# Revit family: Backflow_Preventer-RP-Zurn_Wilkins-Model_950XL3BFSS-(114-2_inch)
name_source: partatom
category: Pipe Accessories
units: mm (PartAtom-declared; Revit-internal decimal feet)

## family parameters
Always vertical = Yes
Cut with Voids When Loaded = No
OmniClass Number = 23.65.55.14.17
OmniClass Title = Adjusting/Controlling Valves for Liquid Services
Part Type = Valve - Breaks Into
Round Connector Dimension = Use Radius
Shared = No
Work Plane-Based = No

## types (3) — shared parameters
Assembly Code = D2020300
BF center = 0' - 0 25/32"
BODY FL BOLT HT = 0' - 0 1/8"
BODY FL HT = 0' - 0 1/4"
BODY FL RADIUS = 0' - 0 9/16"
CB L3 = 0' - 0 1/4"
CB L4 = 0' - 0 1/8"
CB TC DIA1 = 0' - 0 3/8"
CB TC DIA2 = 0' - 0 13/16"
CB TC DIA3 = 0' - 0 3/8"
DIM E - Height (Valve Center to Bottom of relief valve) = 0' - 2 3/4"
Default Elevation = 0' - 0"
Description = Reduced Pressure Principle Assembly
Flow Rate (GPM) = 0 GPM
Hydrostatic Test Pressure = 350.00 psi
LBFV Width = 0' - 3 11/16"
LE to Bf = 0' - 0 5/32"
LEFT BLEND START = 0' - 0 7/16"
Main Material = Paint - Zurn - Bronze
Manufacturer = Zurn Water, LLC
Manufacturer Brand = Zurn Wilkins
Max Working Water Pressure = 175.00 psi
Max Working Water Temperature = 180 °F
Model = 950XL3BFSS
Modified Date = 10/17/25
Product Documentation Link = https://files.zurn.com
Product Installation Sheet URL = https://files.zurn.com
Product Page URL = https://www.zurn.com
Product data URL = https://bimobject.com
REL COV BOLT LG = 0' - 0 1/4"
REL COV REC WID = 0' - 1 5/16"
RIGHT LOFT END = 0' - 1"
RP END = 0' - 4 5/32"
RP FLANGE END = 0' - 0 29/32"
RP PIPE 2 = 0' - 1 1/4"
RP PIPE DIA = 0' - 1"
RP REC THICK = 0' - 1"
RP REC WIDTH = 0' - 1"
Repair Parts URL = https://files.zurn.com
TC H1 = 0' - 1 1/2"
TC H2 = 0' - 0 1/4"
TC H3 = 0' - 1 1/8"
TC RADIUS 1 = 0' - 0 13/32"
TC RADIUS 2 = 0' - 0 3/16"
TC STEM CENTER = 0' - 0 5/8"
TC STEM DIA = 0' - 0 1/2"
TC STEM HT = 0' - 0 17/32"
URL = https://www.zurn.com

## per-type parameters (varying)
- 114-950XL3BFSS (1-1/4" 950XL3BFSS): BFEE=0' - 0 5/16"; BFV Dis=0' - 0"; BFV WIDTH=0' - 3 25/32"; BFVE=0' - 2 1/4"; BODY FL BOLT DIA=0' - 0 9/32"; BODY FL BOLT L1=0' - 2 7/16"; BODY FL BOLT L2=0' - 2 5/8"; BODY FL WID=0' - 3 7/32"; BODY RIB LINE=0' - 2 1/2"; BODY RIB PATH END=0' - 2 1/32"; BODY RIB PATH L1=0' - 1 5/16"; BODY RIB THICK=0' - 0 3/16"; BODY RIB WIDTH=0' - 2 1/4"; BODY TC STEM CENTER=0' - 6"; BTM RIB END=0' - 0 13/32"; BV DIA-1=0' - 1 1/2"; BV DIA-2=0' - 2 1/8"; BV DIA-3=0' - 2 5/16"; BV HEX LENGTH=0' - 0 9/16"; BV HEX WIDTH=0' - 1 29/32"; BV L1=0' - 0 3/4"; BV L2=0' - 1"; BV LENGTH=0' - 3 11/16"; BV RIB HT=0' - 1 1/4"; BV RIB START=0' - 0 1/2"; BV RIB THICK=0' - 0 1/2"; BV RIB WIDTH=0' - 1 13/16"; Butterfly Valve=Fire_Valve-Zurn_Wilkins-Model_F49BR-(114-2_inch) : 114-F49BR (1 1/4" F49BR); CB L1=0' - 0 3/4"; CB L2=0' - 4 1/2"; CB LARGE DIA=0' - 3 1/4"; CB SMALL DIA=0' - 2 1/2"; CB START=0' - 2"; CENTER-END=0' - 7 25/32"; DIM A - Total Length=1' - 1 1/2"; DIM B - Width (Valve end to Valve center)=0' - 3 5/16"; DIM C - Width (Valve center to Valve End)=0' - 1 5/8"; DIM D - Height (Valve Center to top of test cock)=0' - 4 5/16"; HANDLE BASE HT=0' - 2"; HANDLE H1=0' - 0 3/8"; HANDLE HEIGHT=0' - 1"; HANDLE NUT WIDTH=0' - 0 5/8"; HANDLE THICKNESS=0' - 0 1/8"; HANDLE V1=0' - 0 7/8"; HANDLE V2=0' - 5"; LE TO LBFV=0' - 0 1/4"; LEFT BELND LH DIA=0' - 2 5/8"; LEFT BELND RH DIA=0' - 3 1/8"; Length=1' - 3 9/16"; MASKING VER1=0' - 2 3/8"; MASKING VER2=0' - 3"; MR ball valve handle hex width=0' - 0 23/32"; MR left end to ball valve handle-1=0' - 2 9/32"; MR left end to ball valve handle-2=0' - 2 21/32"; MR left end to ball valve handle-3=0' - 2 23/32"; MR left end to main valve-1=0' - 6 5/32"; MR left end to main valve-2=0' - 4 13/16"; MR main valve body diameter-1=0' - 3 1/4"; MR main valve body width-1=0' - 3 31/32"; MR right end to ball valve handle-1=0' - 2 11/32"; MR right end to ball valve handle-2=0' - 2 23/32"; MR right end to ball valve handle-3=0' - 2 25/32"; MR right end to main valve-1=0' - 4 1/2"; MR right end to main valve-2=0' - 4 19/32"; MR valve body diameter-1=0' - 2 5/16"; MR valve body diameter-2=0' - 2 1/8"; MR valve body diameter-3=0' - 1 3/4"; MR valve body diameter-4=0' - 1 1/2"; MR valve center to ball valve handle-1=0' - 1 7/8"; MR valve center to ball valve handle-2=0' - 2 1/16"; MR valve center to ball valve handle-3=0' - 2 5/16"; MR valve center to ball valve handle-4=0' - 2 7/16"; Nominal Diameter=0' - 1 1/4"; Nominal Radius=0' - 0 5/8"; PIPE DIA=0' - 1 1/2"; PIPE RADIUS END=0' - 3 1/16"; Product Weight (lbs)=12; RBFE=0' - 0 13/16"; RBFV Width=0' - 3 19/32"; RBFVE=0' - 3 1/2"; RE to RBFV=0' - 0 3/8"; REL COV BOLT DIA=0' - 0 5/16"; REL COV BOLT HOR C-C=0' - 1 7/8"; REL COV BOLT HOR2 C-C=0' - 3 1/4"; REL COV BOLT VER C-C=0' - 2 3/4"; REL COV REC HT=0' - 1"; RP BTM PIPE DIA=0' - 1 1/8"; RP BTM PIPE L1=0' - 1 1/8"; RP BTM PIPE PLANE=0' - 0 7/8"; RP CENTER=0' - 3 15/32"; RP FLANGE START=0' - 1"; RP LOFT LEFT DIA=0' - 2 7/8"; RP LOFT RIGHT DIA=0' - 1 3/4"; RP REC HT=0' - 1 11/16"; RP START=0' - 4 1/4"; RPC-E=0' - 1 23/32"; TC BASE DIA=0' - 0 3/4"; TC BASE HT=0' - 1 3/8"; TC CENTER=0' - 1 3/4"; TC1 BASE DIA=0' - 0 3/4"; TC1-CENTER=0' - 0 15/16"; TC2 CENTER=0' - 0 5/8"; TC2 STEM CENTER=0' - 3 7/32"; Top Width=0' - 1 1/2"
- 112-950XL3BFSS (1-1/2" 950XL3BFSS): BFEE=0' - 0 1/16"; BFV Dis=0' - 0 1/16"; BFV WIDTH=0' - 3 25/32"; BFVE=0' - 2 1/8"; BODY FL BOLT DIA=0' - 0 9/32"; BODY FL BOLT L1=0' - 2 3/8"; BODY FL BOLT L2=0' - 2 3/8"; BODY FL WID=0' - 3"; BODY RIB LINE=0' - 2 1/2"; BODY RIB PATH END=0' - 1 7/8"; BODY RIB PATH L1=0' - 1 1/4"; BODY RIB THICK=0' - 0 3/16"; BODY RIB WIDTH=0' - 2 1/4"; BODY TC STEM CENTER=0' - 6"; BTM RIB END=0' - 0 13/32"; BV DIA-1=0' - 1 3/4"; BV DIA-2=0' - 2 3/8"; BV DIA-3=0' - 2 9/16"; BV HEX LENGTH=0' - 0 21/32"; BV HEX WIDTH=0' - 2 3/16"; BV L1=0' - 0 5/8"; BV L2=0' - 1 1/8"; BV LENGTH=0' - 4"; BV RIB HT=0' - 1 7/16"; BV RIB START=0' - 0 5/8"; BV RIB THICK=0' - 0 9/16"; BV RIB WIDTH=0' - 2"; Butterfly Valve=Fire_Valve-Zurn_Wilkins-Model_F49BR-(114-2_inch) : 112-F49BR (1 1/2" F49BR); CB L1=0' - 0 5/8"; CB L2=0' - 4 5/8"; CB LARGE DIA=0' - 3"; CB SMALL DIA=0' - 2 1/2"; CB START=0' - 2"; CENTER-END=0' - 7 27/32"; DIM A - Total Length=1' - 1 7/8"; DIM B - Width (Valve end to Valve center)=0' - 3 7/16"; DIM C - Width (Valve center to Valve End)=0' - 1 5/8"; DIM D - Height (Valve Center to top of test cock)=0' - 4 5/16"; HANDLE BASE HT=0' - 2 1/2"; HANDLE H1=0' - 0 7/16"; HANDLE HEIGHT=0' - 1"; HANDLE NUT WIDTH=0' - 0 3/4"; HANDLE THICKNESS=0' - 0 1/8"; HANDLE V1=0' - 1"; HANDLE V2=0' - 5"; LE TO LBFV=0' - 0 1/4"; LEFT BELND LH DIA=0' - 2 5/8"; LEFT BELND RH DIA=0' - 3 1/8"; Length=1' - 3 11/16"; MASKING VER1=0' - 2 1/4"; MASKING VER2=0' - 3 5/16"; MR ball valve handle hex width=0' - 0 7/8"; MR left end to ball valve handle-1=0' - 2 3/8"; MR left end to ball valve handle-2=0' - 2 13/16"; MR left end to ball valve handle-3=0' - 2 7/8"; MR left end to main valve-1=0' - 6 13/32"; MR left end to main valve-2=0' - 5 1/16"; MR main valve body diameter-1=0' - 3 5/32"; MR main valve body width-1=0' - 3 31/32"; MR right end to ball valve handle-1=0' - 2 11/16"; MR right end to ball valve handle-2=0' - 3 1/8"; MR right end to ball valve handle-3=0' - 3 3/16"; MR right end to main valve-1=0' - 4 3/8"; MR right end to main valve-2=0' - 4 9/16"; MR valve body diameter-1=0' - 2 9/16"; MR valve body diameter-2=0' - 2 3/8"; MR valve body diameter-3=0' - 1 7/8"; MR valve body diameter-4=0' - 1 3/4"; MR valve center to ball valve handle-1=0' - 2 3/8"; MR valve center to ball valve handle-2=0' - 2 9/16"; MR valve center to ball valve handle-3=0' - 2 7/8"; MR valve center to ball valve handle-4=0' - 3"; Nominal Diameter=0' - 1 1/2"; Nominal Radius=0' - 0 3/4"; PIPE DIA=0' - 1 3/4"; PIPE RADIUS END=0' - 3 1/16"; Product Weight (lbs)=14; RBFE=0' - 0 19/32"; RBFV Width=0' - 3"; RBFVE=0' - 3"; RE to RBFV=0' - 0 7/16"; REL COV BOLT DIA=0' - 0 5/16"; REL COV BOLT HOR C-C=0' - 1 7/8"; REL COV BOLT HOR2 C-C=0' - 3 1/4"; REL COV BOLT VER C-C=0' - 2 3/4"; REL COV REC HT=0' - 1 1/8"; RP BTM PIPE DIA=0' - 1 1/8"; RP BTM PIPE L1=0' - 1 1/4"; RP BTM PIPE PLANE=0' - 0 7/8"; RP CENTER=0' - 3 15/32"; RP FLANGE START=0' - 1"; RP LOFT LEFT DIA=0' - 2 7/8"; RP LOFT RIGHT DIA=0' - 1 3/4"; RP REC HT=0' - 1 11/16"; RP START=0' - 4 1/2"; RPC-E=0' - 1 23/32"; TC BASE DIA=0' - 0 3/4"; TC BASE HT=0' - 1 7/16"; TC CENTER=0' - 1 3/4"; TC1 BASE DIA=0' - 0 3/4"; TC1-CENTER=0' - 1 1/8"; TC2 CENTER=0' - 0 3/4"; TC2 STEM CENTER=0' - 3 3/16"; Top Width=0' - 1 17/32"
- 2-950XL3BFSS (2" 950XL3BFSS): BFEE=0' - 0 1/32"; BFV Dis=0' - 0 1/4"; BFV WIDTH=0' - 3"; BFVE=0' - 1 31/32"; BODY FL BOLT DIA=0' - 0 3/8"; BODY FL BOLT L1=0' - 2 7/8"; BODY FL BOLT L2=0' - 2 7/8"; BODY FL WID=0' - 3 1/2"; BODY RIB LINE=0' - 3 1/4"; BODY RIB PATH END=0' - 2 9/16"; BODY RIB PATH L1=0' - 1 3/8"; BODY RIB THICK=0' - 0 1/4"; BODY RIB WIDTH=0' - 2"; BODY TC STEM CENTER=0' - 7 5/32"; BTM RIB END=0' - 1 1/8"; BV DIA-1=0' - 2 1/4"; BV DIA-2=0' - 2 7/8"; BV DIA-3=0' - 3"; BV HEX LENGTH=0' - 0 23/32"; BV HEX WIDTH=0' - 2 3/4"; BV L1=0' - 0 7/8"; BV L2=0' - 1 3/8"; BV LENGTH=0' - 4 1/2"; BV RIB HT=0' - 1 11/16"; BV RIB START=0' - 0 13/32"; BV RIB THICK=0' - 0 23/32"; BV RIB WIDTH=0' - 2 1/2"; Butterfly Valve=Fire_Valve-Zurn_Wilkins-Model_F49BR-(114-2_inch) : 2-F49BR (2" F49BR); CB L1=0' - 3 1/2"; CB L2=0' - 3"; CB LARGE DIA=0' - 3 27/32"; CB SMALL DIA=0' - 3 7/16"; CB START=0' - 1 15/16"; CENTER-END=0' - 8 15/16"; DIM A - Total Length=1' - 3 11/16"; DIM B - Width (Valve end to Valve center)=0' - 4 7/16"; DIM C - Width (Valve center to Valve End)=0' - 1 15/16"; DIM D - Height (Valve Center to top of test cock)=0' - 4 15/16"; HANDLE BASE HT=0' - 2 3/4"; HANDLE H1=0' - 0 1/2"; HANDLE HEIGHT=0' - 1 5/32"; HANDLE NUT WIDTH=0' - 0 7/8"; HANDLE THICKNESS=0' - 0 3/16"; HANDLE V1=0' - 1 1/4"; HANDLE V2=0' - 5 3/4"; LE TO LBFV=0' - 0 7/16"; LEFT BELND LH DIA=0' - 3 1/8"; LEFT BELND RH DIA=0' - 3 3/4"; Length=1' - 5 7/8"; MASKING VER1=0' - 2 3/4"; MASKING VER2=0' - 4"; MR ball valve handle hex width=0' - 1"; MR left end to ball valve handle-1=0' - 2 15/16"; MR left end to ball valve handle-2=0' - 3 1/2"; MR left end to ball valve handle-3=0' - 3 9/16"; MR left end to main valve-1=0' - 6 23/32"; MR left end to main valve-2=0' - 5 3/8"; MR main valve body diameter-1=0' - 3 7/8"; MR main valve body width-1=0' - 5 3/16"; MR right end to ball valve handle-1=0' - 2 7/8"; MR right end to ball valve handle-2=0' - 3 7/16"; MR right end to ball valve handle-3=0' - 3 1/2"; MR right end to main valve-1=0' - 4 27/32"; MR right end to main valve-2=0' - 5 1/8"; MR valve body diameter-1=0' - 3 3/16"; MR valve body diameter-2=0' - 2 7/8"; MR valve body diameter-3=0' - 2 5/8"; MR valve body diameter-4=0' - 2 1/4"; MR valve center to ball valve handle-1=0' - 2 19/32"; MR valve center to ball valve handle-2=0' - 2 27/32"; MR valve center to ball valve handle-3=0' - 3 5/32"; MR valve center to ball valve handle-4=0' - 3 11/32"; Nominal Diameter=0' - 2"; Nominal Radius=0' - 1"; PIPE DIA=0' - 2 1/4"; PIPE RADIUS END=0' - 2 5/8"; Product Weight (lbs)=18; RBFE=0' - 0 1/2"; RBFV Width=0' - 3 19/32"; RBFVE=0' - 2 1/4"; RE to RBFV=0' - 0 3/8"; REL COV BOLT DIA=0' - 0 13/32"; REL COV BOLT HOR C-C=0' - 2 9/16"; REL COV BOLT HOR2 C-C=0' - 4 13/32"; REL COV BOLT VER C-C=0' - 3 1/2"; REL COV REC HT=0' - 1 1/2"; RP BTM PIPE DIA=0' - 1 3/8"; RP BTM PIPE L1=0' - 1 5/8"; RP BTM PIPE PLANE=0' - 1 3/8"; RP CENTER=0' - 4 3/8"; RP FLANGE START=0' - 1 1/8"; RP LOFT LEFT DIA=0' - 3 1/2"; RP LOFT RIGHT DIA=0' - 2 1/2"; RP REC HT=0' - 1 29/32"; RP START=0' - 4 11/16"; RPC-E=0' - 2 1/4"; TC BASE DIA=0' - 0 7/8"; TC BASE HT=0' - 1 13/16"; TC CENTER=0' - 1 27/32"; TC1 BASE DIA=0' - 0 7/8"; TC1-CENTER=0' - 0 7/8"; TC2 CENTER=0' - 1 1/4"; TC2 STEM CENTER=0' - 4"; Top Width=0' - 1 15/16"

## geometry (parser evidence)
native form markers: Sweep x9
no freeform markers — native parametric forms only
